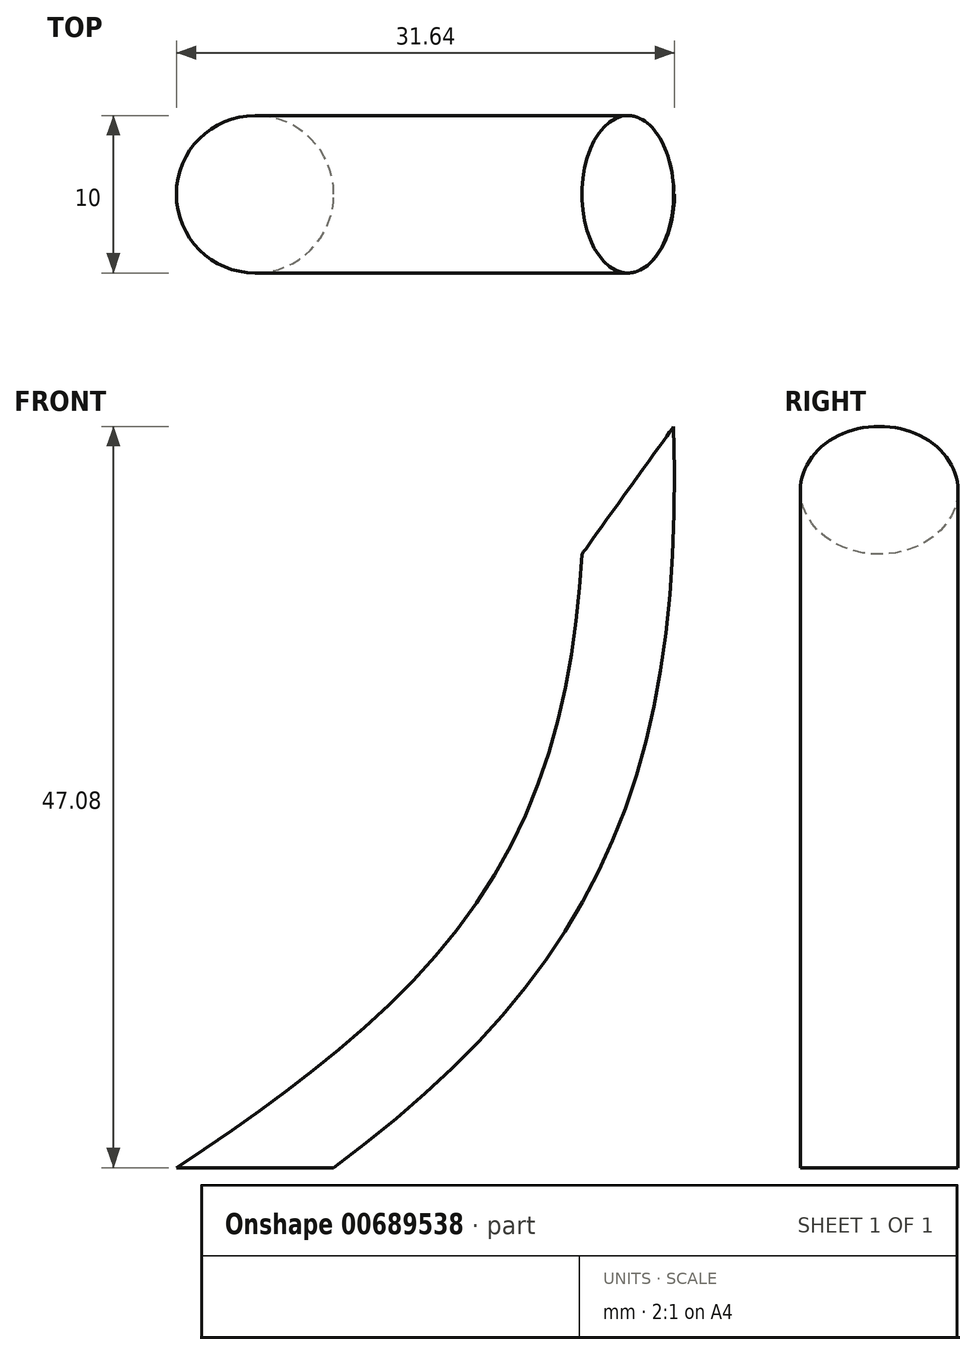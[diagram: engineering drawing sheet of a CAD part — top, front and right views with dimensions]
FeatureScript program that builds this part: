
annotation { "Feature Type Name" : "Feature", "Feature Type Description" : "" }
export const myFeature = defineFeature(function(context is Context, id is Id, definition is map)
    precondition{}
    {
        {
            var Q0;
            Q0=qCreatedBy(makeId("Front.planeOp"),FACE);
            var sketch = newSketch(context, id + "F0", { "sketchPlane" : qUnion([Q0])});
            skFitSpline(sketch, "E0", {"points": [v(0, 0) * mm, v(23.67, 43.02) * mm], "startDerivative": vector(47.94, 33.59) * mm, "endDerivative": vector(0.75, 64.15) * mm});
            skSolve(sketch);
        }
        {
            var Q0;
            Q0=qCreatedBy(makeId("Top.planeOp"),FACE);
            var sketch = newSketch(context, id + "F1", { "sketchPlane" : qUnion([Q0])});
            skCircle(sketch, "E1", {"center": v(0, 0) * mm, "radius": 5 * mm});
            skSolve(sketch);
        }
        {
            var Q0;
            Q0=makeQuery(id+"F1.imprint","IMPRINT",FACE,{"disambiguationData":[TD([[makeQuery(id+"F1.imprint","IMPRINT",EDGE,{"derivedFrom":sQuery(id+"F1.wireOp",EDGE,"E1")}),1.0]])]});
            var Q1;
            Q1=sQuery(id+"F0.wireOp",EDGE,"E0");
            sweep(context, id + "F2", {"profiles" : qUnion([Q0]), "path" : qUnion([Q1])});
        }
    });
